# Revit family: 303_R411X_+R460
name_source: partatom
category: Pipe Accessories
revit_build: Autodesk Revit 2018 (Build: 20170223_1515(x64)
units: mm (PartAtom-declared; Revit-internal decimal feet)

## family parameters
Always vertical = Yes
Cut with Voids When Loaded = No
Part Type = Valve - Breaks Into
Round Connector Dimension = Use Diameter
Shared = No
Work Plane-Based = No

## types (3) — shared parameters
CAT0 = Yes
CenSd_W2_6 = 13 mm  [stored 0.0426509 ft]
Description = Angle valve with thermostatic option, with connection for adaptor, with cover to protect body before assembling
H3 = 4 mm  [stored 0.0131234 ft]
H3__ve = -4 mm  [stored -0.0131234 ft]
H4 = 1 mm  [stored 0.00328084 ft]
J1 = 6 mm  [stored 0.019685 ft]
J2 = 2 mm  [stored 0.00656168 ft]
J4 = 6 mm  [stored 0.019685 ft]
J5 = 6 mm  [stored 0.019685 ft]
L = 40 mm  [stored 0.131234 ft]
L2 = 53 mm
L2D = 40 mm  [stored 0.131234 ft]
L2D_Min = 3048 mm  [stored 10 ft]
L3 = 9 mm  [stored 0.0295276 ft]
L3__ve = -9 mm  [stored -0.0295276 ft]
L4 = 9 mm  [stored 0.0295276 ft]
L4__ve = -9 mm  [stored -0.0295276 ft]
L5 = 5 mm  [stored 0.0164042 ft]
L5__ve = -5 mm  [stored -0.0164042 ft]
M22 = 6 mm  [stored 0.019685 ft]
M3 = 14 mm  [stored 0.0459318 ft]
M3__ve = -14 mm
Manufacturer = Giacomini
QmdConnectorList = 301;D;302;D1
TH2 = 76 mm
TR1 = 15 mm  [stored 0.0492126 ft]
URL = http://www.giacomini.com
W1 = 12 mm  [stored 0.0393701 ft]
W2 = 15 mm  [stored 0.0492126 ft]
X4 = 6 mm  [stored 0.019685 ft]
magiPartTypeId = 303
magiProductFamilyId = R411X*+R460
zero-valued in all types: MC_Default_elevation

## per-type parameters (varying)
| type | B1 | B4 | D | D1 | G3 | R1 | W2D |
| R411X032+R460 | 4 mm  [stored 0.0131234 ft] | 7 mm  [stored 0.0229659 ft] | 16 mm | 10 mm | 7 mm  [stored 0.0229659 ft] | 5 mm  [stored 0.0164042 ft] | 16 mm  [stored 0.0524934 ft] |
| R411X034+R460 | 5 mm  [stored 0.0164042 ft] | 8 mm  [stored 0.0262467 ft] | 18 mm | 15 mm | 9 mm  [stored 0.0295276 ft] | 8 mm  [stored 0.0262467 ft] | 18 mm |
| R411X033+R460 | 4 mm  [stored 0.0131234 ft] | 7 mm  [stored 0.0229659 ft] | 16 mm | 15 mm | 9 mm  [stored 0.0295276 ft] | 8 mm  [stored 0.0262467 ft] | 16 mm  [stored 0.0524934 ft] |

note: column(s) folded — value = type name in every type: magiProductCode, magiProductId

note: [stored X ft] marks values corroborated as IEEE doubles in the binary element streams (Revit-internal decimal feet)

## geometry (parser evidence)
native form markers: Sweep x2
no freeform markers — native parametric forms only
